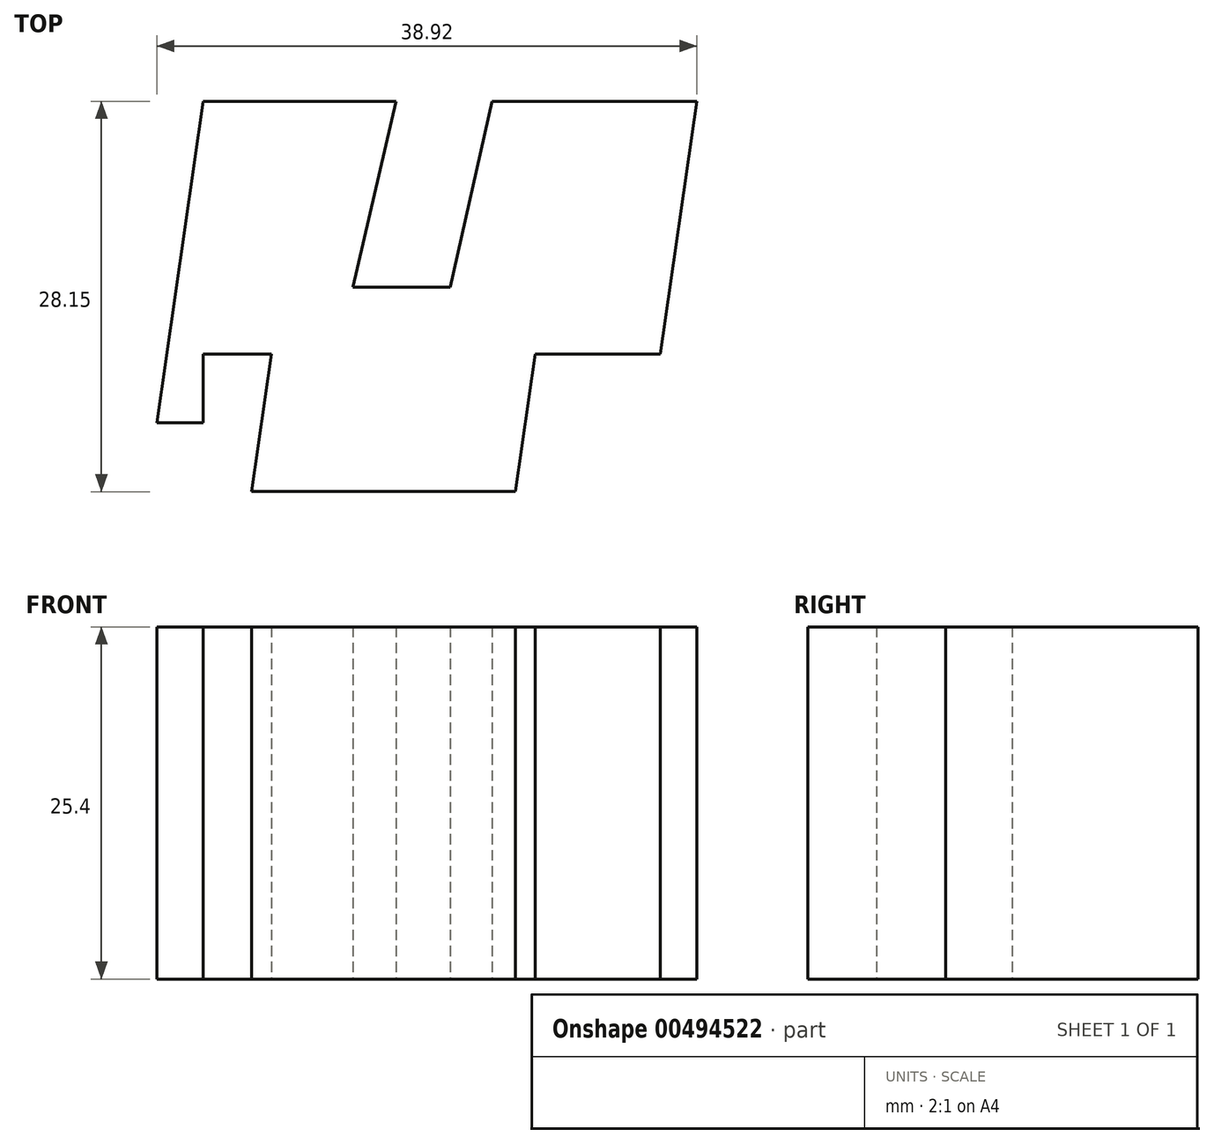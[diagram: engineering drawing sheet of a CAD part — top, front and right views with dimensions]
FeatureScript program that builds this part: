
annotation { "Feature Type Name" : "Feature", "Feature Type Description" : "" }
export const myFeature = defineFeature(function(context is Context, id is Id, definition is map)
    precondition{}
    {
        {
            var Q0;
            Q0=qCreatedBy(makeId("Top.planeOp"),FACE);
            var sketch = newSketch(context, id + "F0", { "sketchPlane" : qUnion([Q0])});
            skLineSegment(sketch, "E0", {"start": v(7.3, -49.35) * mm, "end": v(28.04, -23.27) * mm});
            skLineSegment(sketch, "E1", {"start": v(28.04, -23.27) * mm, "end": v(-7.55, -23.27) * mm});
            skLineSegment(sketch, "E2", {"start": v(-7.55, -23.27) * mm, "end": v(7.3, -49.35) * mm});
            skLineSegment(sketch, "E3", {"start": v(28.04, -23.27) * mm, "end": v(32.1, 4.88) * mm});
            skLineSegment(sketch, "E4", {"start": v(32.1, 4.88) * mm, "end": v(-3.48, 4.88) * mm});
            skLineSegment(sketch, "E5", {"start": v(-7.55, -23.27) * mm, "end": v(-3.48, 4.88) * mm});
            skLineSegment(sketch, "E6", {"start": v(17.32, 4.88) * mm, "end": v(14.3, -8.53) * mm});
            skPoint(sketch, "E6.endSnap0", {"position": v(14.3, 4.88) * mm});
            skLineSegment(sketch, "E7", {"start": v(14.3, -8.53) * mm, "end": v(7.3, -8.53) * mm});
            skLineSegment(sketch, "E8", {"start": v(7.3, -8.53) * mm, "end": v(10.42, 4.88) * mm});
            skLineSegment(sketch, "E9", {"start": v(29.47, -13.34) * mm, "end": v(20.43, -13.34) * mm});
            skLineSegment(sketch, "E10", {"start": v(20.43, -13.34) * mm, "end": v(19, -23.27) * mm});
            skLineSegment(sketch, "E11", {"start": v(0, -23.27) * mm, "end": v(1.43, -13.34) * mm});
            skLineSegment(sketch, "E12", {"start": v(1.43, -13.34) * mm, "end": v(-3.48, -13.34) * mm});
            skLineSegment(sketch, "E13", {"start": v(-3.48, -23.27) * mm, "end": v(-3.48, -13.34) * mm});
            skLineSegment(sketch, "E14", {"start": v(0.71, -18.3) * mm, "end": v(-7.55, -18.3) * mm});
            skLineSegment(sketch, "E15", {"start": v(24.3, -23.27) * mm, "end": v(29.47, -13.34) * mm});
            skLineSegment(sketch, "E16", {"start": v(26.88, -18.3) * mm, "end": v(20.43, -18.3) * mm});
            skSolve(sketch);
        }
        {
            var Q0;
            {var subQ8=sQuery(id+"F0.wireOp",EDGE,"E6");Q0=makeQuery(id+"F0.imprint","IMPRINT",FACE,{"disambiguationData":[TD([[makeQuery(id+"F0.imprint","IMPRINT",EDGE,{"derivedFrom":subQ8}),1.0]])]});}
            extrude(context, id + "F1", {"entities" : qUnion([Q0]), "depth" : 25.4 * mm});
        }
        {
            var Q0;
            Q0=makeQuery(id+"F1.opExtrude","SWEPT_FACE",FACE,{"disambiguationData":[OSD([sQuery(id+"F0.wireOp",EDGE,"E3")])]});
            var sketch = newSketch(context, id + "F2", { "sketchPlane" : qUnion([Q0])});
            skCircle(sketch, "E17", {"center": v(0, 12.07) * mm, "radius": 4.12 * mm});
            skSolve(sketch);
        }
        {
            var Q0;
            Q0=makeQuery(id+"F2.imprint","IMPRINT",FACE,{"disambiguationData":[TD([[makeQuery(id+"F2.imprint","IMPRINT",EDGE,{"derivedFrom":sQuery(id+"F2.wireOp",EDGE,"E17")}),1.0]])]});
            extrude(context, id + "F3", {"entities" : qUnion([Q0]), "operationType" : NewBodyOperationType.REMOVE, "depth" : 19.05 * mm});
        }
    });
